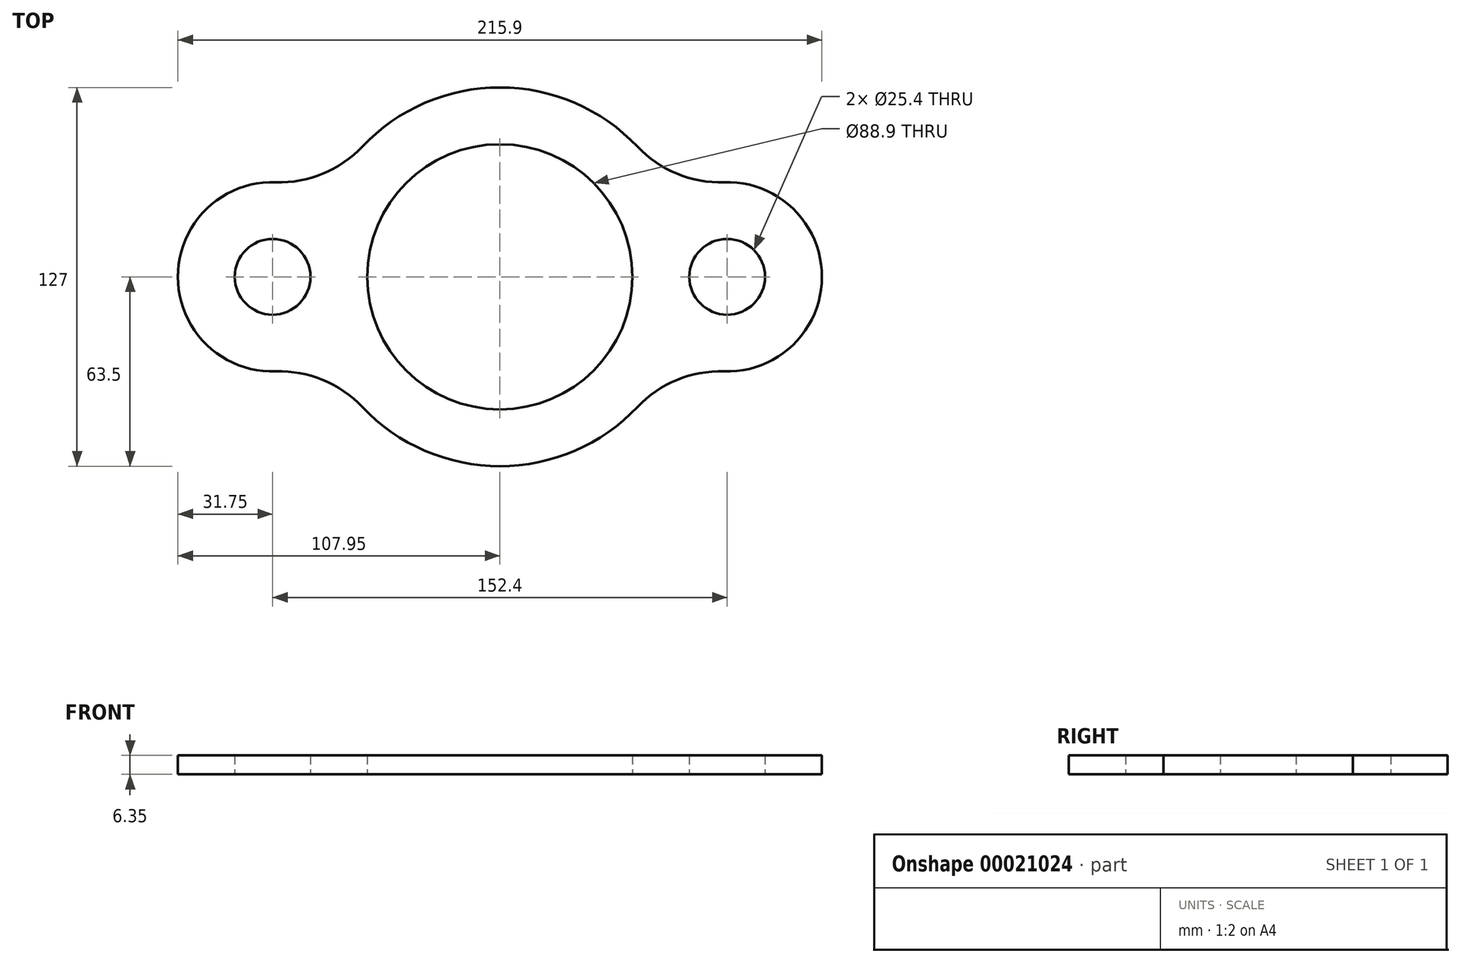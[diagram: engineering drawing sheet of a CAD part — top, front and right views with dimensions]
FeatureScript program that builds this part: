
annotation { "Feature Type Name" : "Feature", "Feature Type Description" : "" }
export const myFeature = defineFeature(function(context is Context, id is Id, definition is map)
    precondition{}
    {
        {
            var Q0;
            Q0=qCreatedBy(makeId("Top.planeOp"),FACE);
            var sketch = newSketch(context, id + "F0", { "sketchPlane" : qUnion([Q0])});
            skCircle(sketch, "E0", {"center": v(0, 0) * mm, "radius": 44.45 * mm});
            skCircle(sketch, "E1", {"center": v(76.2, 0) * mm, "radius": 12.7 * mm});
            skCircle(sketch, "E2", {"center": v(-76.2, 0) * mm, "radius": 12.7 * mm});
            skArc(sketch, "E3", {"start": v(-75.12, 31.73) * mm, "mid": v(-107.95, 0) * mm, "end": v(-75.12, -31.73) * mm});
            skArc(sketch, "E4", {"start": v(75.12, -31.73) * mm, "mid": v(107.95, 0) * mm, "end": v(75.12, 31.73) * mm});
            skArc(sketch, "E5", {"start": v(-46.14, -43.63) * mm, "mid": v(0, -63.5) * mm, "end": v(46.14, -43.63) * mm});
            skArc(sketch, "E6", {"start": v(-75.12, 31.73) * mm, "mid": v(-59.35, 34.56) * mm, "end": v(-46.14, 43.63) * mm});
            skArc(sketch, "E7", {"start": v(46.14, 43.63) * mm, "mid": v(59.35, 34.56) * mm, "end": v(75.12, 31.73) * mm});
            skArc(sketch, "E8", {"start": v(-46.14, -43.63) * mm, "mid": v(-59.35, -34.56) * mm, "end": v(-75.12, -31.73) * mm});
            skArc(sketch, "E9", {"start": v(75.12, -31.73) * mm, "mid": v(59.35, -34.56) * mm, "end": v(46.14, -43.63) * mm});
            skArc(sketch, "E10.trimOffspring", {"start": v(46.14, 43.63) * mm, "mid": v(0, 63.5) * mm, "end": v(-46.14, 43.63) * mm});
            skSolve(sketch);
        }
        {
            var Q0;
            Q0=makeQuery(id+"F0.imprint","IMPRINT",FACE,{"disambiguationData":[TD([[makeQuery(id+"F0.imprint","IMPRINT",EDGE,{"derivedFrom":sQuery(id+"F0.wireOp",EDGE,"E0")}),-1.0]])]});
            extrude(context, id + "F1", {"entities" : qUnion([Q0]), "depth" : 6.35 * mm});
        }
    });
